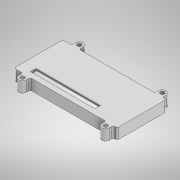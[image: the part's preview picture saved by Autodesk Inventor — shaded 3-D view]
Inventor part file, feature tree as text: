
AUTODESK INVENTOR PART (.ipt)
format: ipt  version: 2021 (Build 250183000, 183)  size: 542,720 bytes
history: native  units: mm
features: sketch x10, extrude x9, fillet x3, projected_geometry x3
ambient origin geometry x8: Origin, YZ Plane, XZ Plane, XY Plane, X Axis, Y Axis, Z Axis, Center Point
bodies: Solid1 (feature_tree)
feature tree (25):
  extrude  "Extrusion1"  Depth=30.0mm
  extrude  "Extrusion2"  Depth=1.0mm
  fillet  "Fillet2"  Radius=1.0mm
  extrude  "Extrusion5"  Depth=6.0mm
  extrude  "Extrusion15"  Depth=1.0mm
  fillet  "Fillet4"  Radius=1.0mm
  extrude  "Extrusion16"  Depth=1.0mm
  fillet  "Fillet5"  Radius=117.5mm
  sketch  "Sketch15"  dims[d13=2.0mm d14=2.0mm]
  extrude  "Extrusion17"  Depth=2.0mm
  extrude  "Extrusion18"  Depth=1.0mm
  extrude  "Extrusion20"  Depth=2.0mm
  extrude  "Extrusion21"  Depth=2.0mm
  sketch  "Sketch1"  dims[d0=37.0mm d1=30.0mm]
  sketch  "Sketch2"  dims[d2=18.0mm d3=37.5mm d4=1.0mm]
  projected_geometry  "Projected Loop1"
  sketch  "Sketch5"  dims[d5=6.0mm d6=17.5mm]
  sketch  "Sketch13"  dims[d7=28.0mm d8=1.0mm d9=1.0mm]
  sketch  "Sketch14"  dims[d10=1.0mm d11=1.0mm d12=117.5mm]
  sketch  "Sketch16"  dims[d15=1.0mm d16=1.0mm]
  projected_geometry  "Projected Loop4"
  sketch  "Sketch17"  dims[d17=2.0mm d18=2.0mm]
  projected_geometry  "Projected Loop5"
  sketch  "Sketch18"  dims[d19=2.0mm d20=2.0mm]
  sketch  "Sketch20"  dims[d21=2.5mm d22=2.5mm d23=5.0mm d24=2.5mm d25=2.5mm d26=2.5mm d27=2.5mm d28=5.0mm d29=5.0mm d30=2.5mm d31=3.1mm d32=3.1mm d33=3.1mm d34=3.1mm d35=3.1mm d36=3.1mm d37=7.0mm d38=0.0mm d39=1.0mm d40=0.0mm d44=1.0mm d45=1.0mm d46=0.5mm d47=0.0mm d48=1.0mm d49=1.0mm d50=1.0mm d51=1.0mm d53=1.0mm d61=7.0mm d62=0.0mm d114=2.0mm d115=2.0mm d116=2.0mm d117=53.0mm d118=50.0mm d119=10.0mm d120=2.5mm d121=5.0mm d122=12.0mm d123=9.5mm d124=20.0mm d125=0.0mm d126=2.0mm d127=2.0mm d128=10.0mm d129=0.0mm d130=2.0mm d131=5.0mm d132=0.0mm d133=1.0mm d134=0.0mm d147=3.5mm d148=7.0mm d149=7.5mm d150=18.0mm d151=10.0mm d152=0.0mm d153=2.7mm d154=2.7mm d155=2.7mm d156=2.7mm d157=10.0mm d158=0.0mm]
